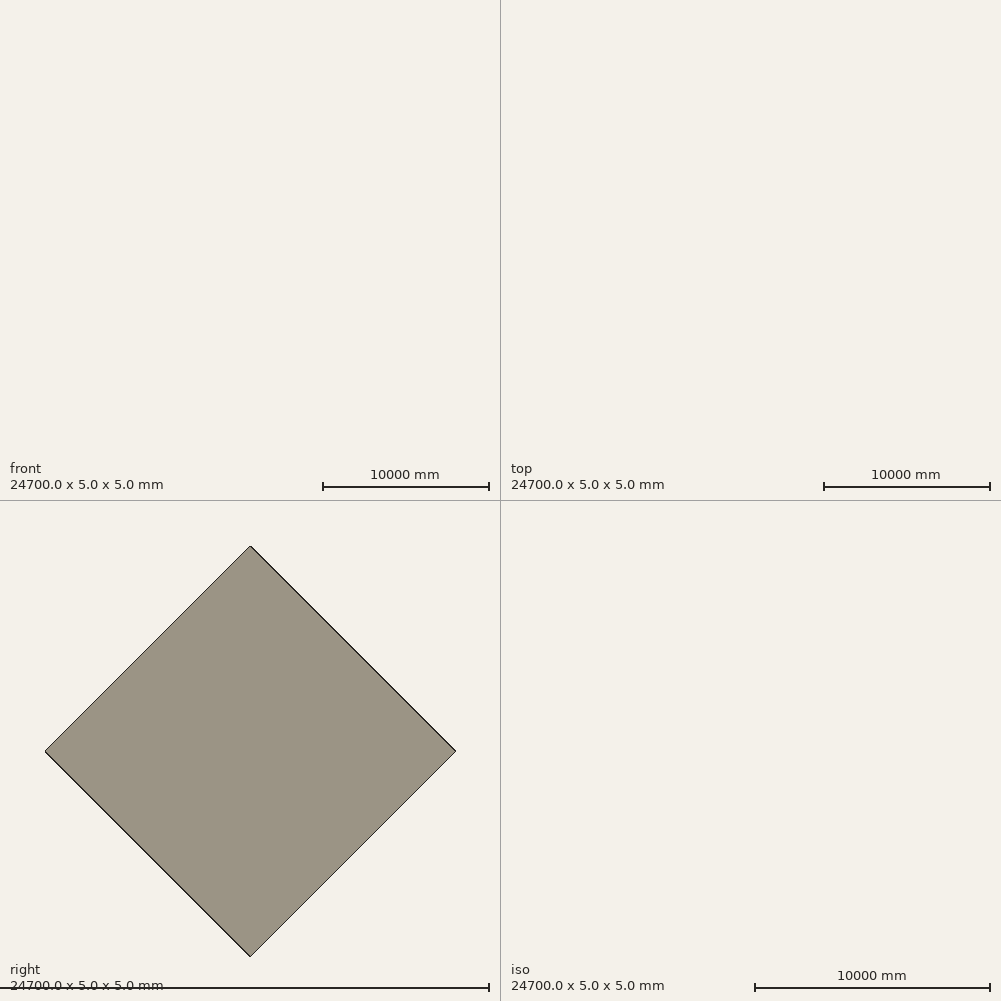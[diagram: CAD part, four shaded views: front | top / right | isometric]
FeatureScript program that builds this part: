
annotation { "Feature Type Name" : "Feature", "Feature Type Description" : "" }
export const myFeature = defineFeature(function(context is Context, id is Id, definition is map)
    precondition{}
    {
        {
            var Q0;
            Q0=qCreatedBy(makeId("Right.planeOp"),FACE);
            var sketch = newSketch(context, id + "F0", { "sketchPlane" : qUnion([Q0])});
            skCircle(sketch, "E0", {"center": v(0, 0) * mm, "radius": 2.5 * mm});
            skSolve(sketch);
        }
        {
            var Q0;
            Q0=qSketchRegion(id+"F0",true);
            extrude(context, id + "F1", {"entities" : qUnion([Q0]), "depth" : 24700 * mm, "offsetDistance" : 25 * mm});
        }
    });
